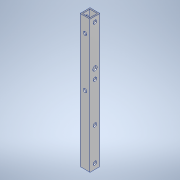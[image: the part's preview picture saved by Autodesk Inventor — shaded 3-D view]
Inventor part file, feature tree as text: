
AUTODESK INVENTOR PART (.ipt)
format: ipt  version: 2020.3 (Build 243373000, 373)  size: 145,408 bytes
history: native  units: mm
features: sketch x5, hole x4, other x1, extrude x1
ambient origin geometry x8: Origin, YZ Plane, XZ Plane, XY Plane, X Axis, Y Axis, Z Axis, Center Point
bodies: Body1 (feature_tree)
feature tree (11):
  other  "ソリッド1"
  extrude  "押し出し1"  Depth=9.0mm
  hole  "穴1"  [1 undecoded]
  hole  "穴2"  [1 undecoded]
  hole  "穴3"  [1 undecoded]
  hole  "穴4"  [1 undecoded]
  sketch  "スケッチ1"
  sketch  "スケッチ2"
  sketch  "スケッチ3"
  sketch  "スケッチ4"
  sketch  "スケッチ5"
note: 4 required parameter values undecoded (feature->parameter linkage not recoverable at this tier; creation-order binding heuristic only, values carry confidence <= 0.55)
